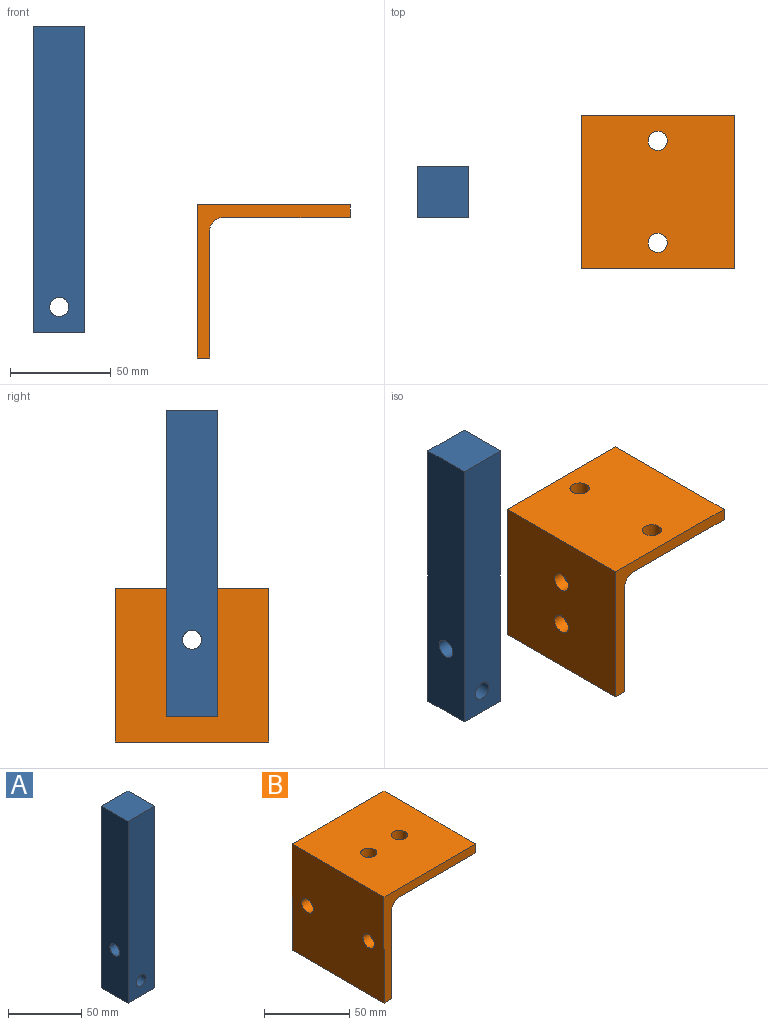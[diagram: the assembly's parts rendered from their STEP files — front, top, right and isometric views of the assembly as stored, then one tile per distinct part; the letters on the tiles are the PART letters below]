
ASSEMBLY  parts=2 mates=2
PART A: 8 faces, bbox 25.4x25.4x152.4 mm
  f0: plane 152.4x25.4mm, normal (0,1,0), area 3799.7mm2, adj f1,f3,f4,f5,f6
  f1: plane 152.4x25.4mm, normal (-1,0,0), area 3799.7mm2, adj f0,f2,f4,f5,f7
  f2: plane 152.4x25.4mm, normal (0,-1,0), area 3799.7mm2, adj f1,f3,f4,f5,f6
  f3: plane 152.4x25.4mm, normal (1,0,0), area 3799.7mm2, adj f0,f2,f4,f5,f7
  f4: plane 25.4x25.4mm, normal (0,0,1), area 645.2mm2, adj f0,f1,f2,f3
  f5: plane 25.4x25.4mm, normal (0,0,-1), area 645.2mm2, adj f0,f1,f2,f3
  f6: cylinder r=4.76mm len=25.4mm, axis (0,-1,0), area 760.1mm2, adj f0,f2
  f7: cylinder r=4.76mm len=25.4mm, axis (-1,0,0), area 760.1mm2, adj f1,f3
PART B: 13 faces, bbox 76.2x76.2x76.2 mm
  f0: plane 76.2x76.2mm, normal (0,0,1), area 5663.9mm2, adj f1,f6,f7,f8,f11,f12
  f1: plane 76.2x76.2mm, normal (-1,0,0), area 5663.9mm2, adj f0,f2,f7,f8,f9,f10
  f2: plane 76.2x6.35mm, normal (0,0,-1), area 483.9mm2, adj f1,f3,f7,f8
  f3: plane 76.2x63.5mm, normal (1,0,0), area 4696.2mm2, adj f2,f4,f7,f8,f9,f10
  f4: cylinder r=6.35mm len=76.2mm, axis (0,1,0), area 760.1mm2, adj f3,f5,f7,f8
  f5: plane 76.2x63.5mm, normal (0,0,-1), area 4696.2mm2, adj f4,f6,f7,f8,f11,f12
  f6: plane 76.2x6.35mm, normal (1,0,0), area 483.9mm2, adj f0,f5,f7,f8
  f7: plane 76.2x76.2mm, normal (0,-1,0), area 936.1mm2, adj f0,f1,f2,f3,f4,f5,f6
  f8: plane 76.2x76.2mm, normal (0,1,0), area 936.1mm2, adj f0,f1,f2,f3,f4,f5,f6
  f9: cylinder r=4.76mm len=9.53mm, axis (-1,0,0), area 190mm2, adj f1,f3
  f10: cylinder r=4.76mm len=9.53mm, axis (-1,0,0), area 190mm2, adj f1,f3
  f11: cylinder r=4.76mm len=9.53mm, axis (0,0,1), area 190mm2, adj f0,f5
  f12: cylinder r=4.76mm len=9.53mm, axis (0,0,1), area 190mm2, adj f0,f5
PLACE A t=(-54.21,47.14,5.66)mm fixed
PLACE B rot(axis=(0.71,0,-0.71),180deg) t=(14.31,9.04,-7.04)mm
MATE cylindrical B.f11 <-> A.f7  axis (1,0,0) through (20.66,47.14,-32.44)mm
MATE parallel B.f1 <-> A.f5  axis (0,0,1) through (52.41,47.14,-7.04)mm
